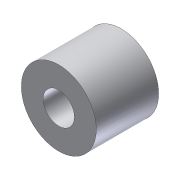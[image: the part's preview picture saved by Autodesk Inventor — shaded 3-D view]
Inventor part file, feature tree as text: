
AUTODESK INVENTOR PART (.ipt)
format: ipt  version: 2012 (Build 160160000, 160)  size: 80,384 bytes
history: native  units: in
note: dims shown in document units (in); Inventor stores cm internally (conversion verified against a paired STEP export)
features: extrude x1, sketch x1
ambient origin geometry x8: Origin, YZ Plane, XZ Plane, XY Plane, X Axis, Y Axis, Z Axis, Center Point
bodies: Solid1 (feature_tree)
feature tree (2):
  extrude  "Extrusion1"  Depth=0.625in
  sketch  "Sketch1"  dims[d0=1.5in d1=0.625in d2=1.25in d3=0.0in]
